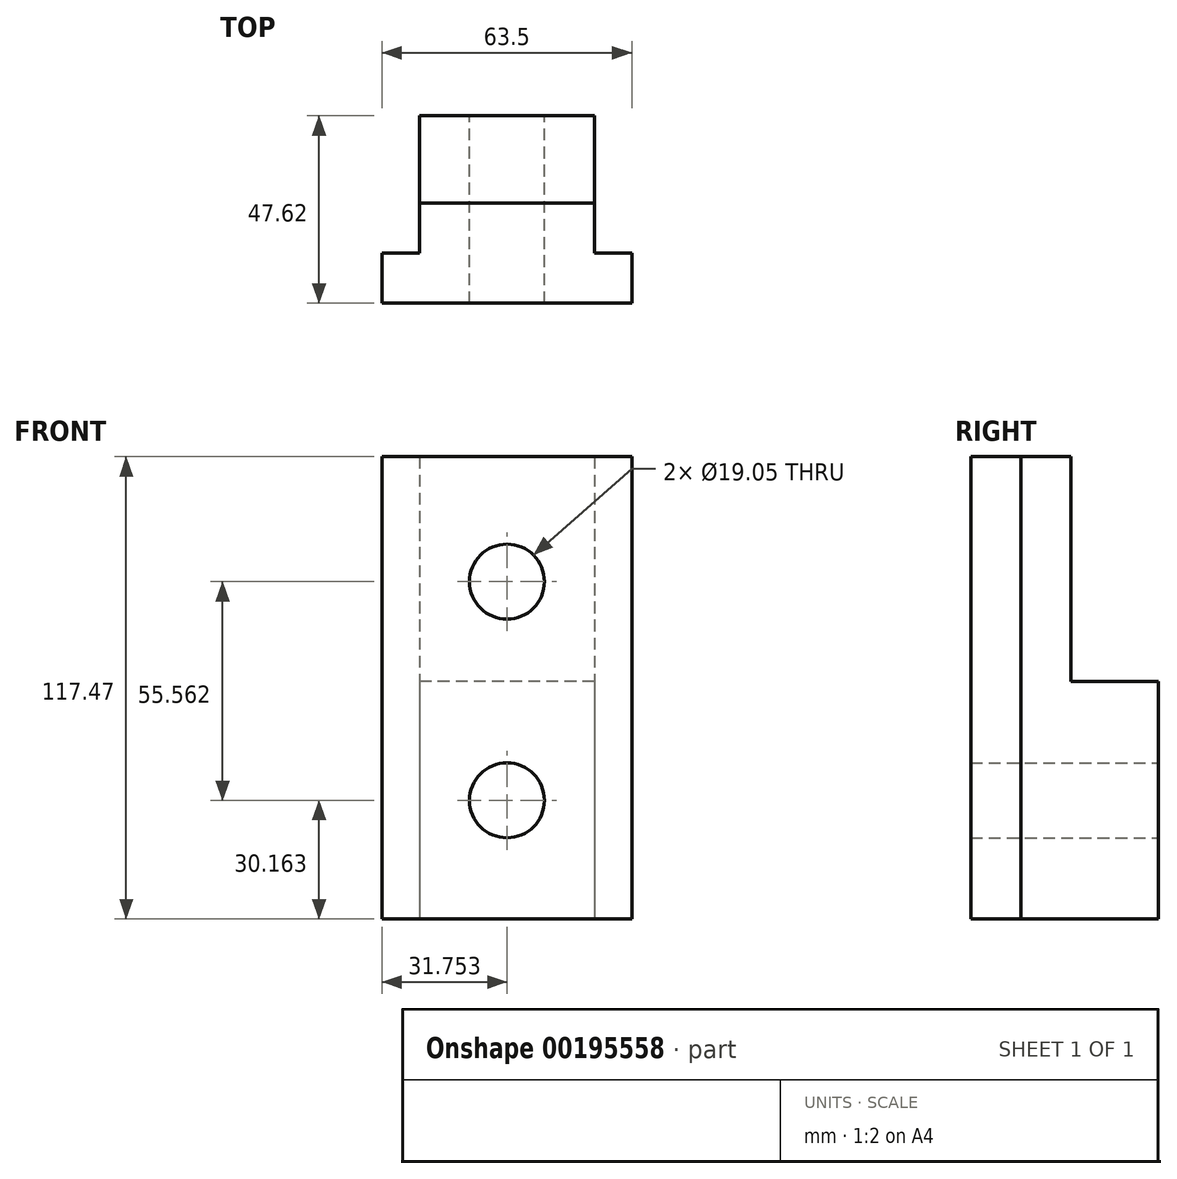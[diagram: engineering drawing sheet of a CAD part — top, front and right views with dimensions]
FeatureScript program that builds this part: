
annotation { "Feature Type Name" : "Feature", "Feature Type Description" : "" }
export const myFeature = defineFeature(function(context is Context, id is Id, definition is map)
    precondition{}
    {
        {
            var Q0;
            Q0=qCreatedBy(makeId("Top.planeOp"),FACE);
            var sketch = newSketch(context, id + "F0", { "sketchPlane" : qUnion([Q0])});
            skLineSegment(sketch, "E0", {"start": v(-41.13, -16.72) * mm, "end": v(22.37, -16.72) * mm});
            skLineSegment(sketch, "E1", {"start": v(22.37, -16.72) * mm, "end": v(22.37, -4.02) * mm});
            skLineSegment(sketch, "E2", {"start": v(-41.13, -16.72) * mm, "end": v(-41.13, -4.02) * mm});
            skLineSegment(sketch, "E3", {"start": v(22.37, -4.02) * mm, "end": v(12.85, -4.02) * mm});
            skLineSegment(sketch, "E4", {"start": v(-41.13, -4.02) * mm, "end": v(-31.6, -4.02) * mm});
            skLineSegment(sketch, "E5", {"start": v(-31.6, -4.02) * mm, "end": v(-31.6, 8.68) * mm});
            skLineSegment(sketch, "E6", {"start": v(12.85, -4.02) * mm, "end": v(12.85, 8.68) * mm});
            skLineSegment(sketch, "E7", {"start": v(-31.6, 8.68) * mm, "end": v(12.85, 8.68) * mm});
            skSolve(sketch);
        }
        {
            var Q0;
            Q0=makeQuery(id+"F0.imprint","IMPRINT",FACE,{"disambiguationData":[TD([[makeQuery(id+"F0.imprint","IMPRINT",EDGE,{"derivedFrom":sQuery(id+"F0.wireOp",EDGE,"E0")}),1.0]])]});
            extrude(context, id + "F1", {"entities" : qUnion([Q0]), "depth" : 117.47 * mm});
        }
        {
            var Q0;
            Q0=makeQuery(id+"F1.opExtrude","SWEPT_FACE",FACE,{"disambiguationData":[OSD([sQuery(id+"F0.wireOp",EDGE,"E7")])]});
            var sketch = newSketch(context, id + "F2", { "sketchPlane" : qUnion([Q0])});
            skLineSegment(sketch, "E8", {"start": v(-12.85, 0) * mm, "end": v(-12.85, 60.33) * mm});
            skLineSegment(sketch, "E9", {"start": v(-12.85, 60.33) * mm, "end": v(31.6, 60.33) * mm});
            skLineSegment(sketch, "E10", {"start": v(31.6, 0) * mm, "end": v(31.6, 60.33) * mm});
            skSolve(sketch);
        }
        {
            var Q0;
            Q0=makeQuery(id+"F2.imprint","IMPRINT",FACE,{"disambiguationData":[TD([[makeQuery(id+"F2.imprint","IMPRINT",EDGE,{"derivedFrom":sQuery(id+"F2.wireOp",EDGE,"E8")}),1.0]])]});
            extrude(context, id + "F3", {"entities" : qUnion([Q0]), "operationType" : NewBodyOperationType.ADD, "depth" : 22.22 * mm});
        }
        {
            var Q0;
            Q0=makeQuery(id+"F1.opExtrude","SWEPT_FACE",FACE,{"disambiguationData":[OSD([sQuery(id+"F0.wireOp",EDGE,"E7")])]});
            var sketch = newSketch(context, id + "F4", { "sketchPlane" : qUnion([Q0])});
            skCircle(sketch, "E11", {"center": v(9.38, 85.73) * mm, "radius": 9.53 * mm});
            skSolve(sketch);
        }
        {
            var Q0;
            Q0=makeQuery(id+"F4.imprint","IMPRINT",FACE,{"disambiguationData":[TD([[makeQuery(id+"F4.imprint","IMPRINT",EDGE,{"derivedFrom":sQuery(id+"F4.wireOp",EDGE,"E11")}),1.0]])]});
            extrude(context, id + "F5", {"entities" : qUnion([Q0]), "operationType" : NewBodyOperationType.REMOVE, "endBound" : BoundingType.THROUGH_ALL, "oppositeDirection" : true, "depth" : 25.4 * mm});
        }
        {
            var Q0;
            Q0=makeQuery(id+"F3.opExtrude","CAP_FACE",FACE,{"disambiguationData":[OSD([sQuery(id+"F0.wireOp",EDGE,"E7"),sQuery(id+"F2.wireOp",EDGE,"E8"),sQuery(id+"F2.wireOp",EDGE,"E9"),sQuery(id+"F2.wireOp",EDGE,"E10")])],"isStart":false});
            var sketch = newSketch(context, id + "F6", { "sketchPlane" : qUnion([Q0])});
            skLineSegment(sketch, "E12", {"start": v(-12.85, 0) * mm, "end": v(-12.85, 30.16) * mm});
            skLineSegment(sketch, "E13", {"start": v(31.6, 0) * mm, "end": v(9.38, 0) * mm});
            skCircle(sketch, "E14", {"center": v(9.38, 30.16) * mm, "radius": 9.53 * mm});
            skSolve(sketch);
        }
        {
            var Q0;
            Q0=makeQuery(id+"F6.imprint","IMPRINT",FACE,{"disambiguationData":[TD([[makeQuery(id+"F6.imprint","IMPRINT",EDGE,{"derivedFrom":sQuery(id+"F6.wireOp",EDGE,"E14")}),1.0]])]});
            extrude(context, id + "F7", {"entities" : qUnion([Q0]), "operationType" : NewBodyOperationType.REMOVE, "endBound" : BoundingType.THROUGH_ALL, "oppositeDirection" : true, "depth" : 25.4 * mm});
        }
    });
